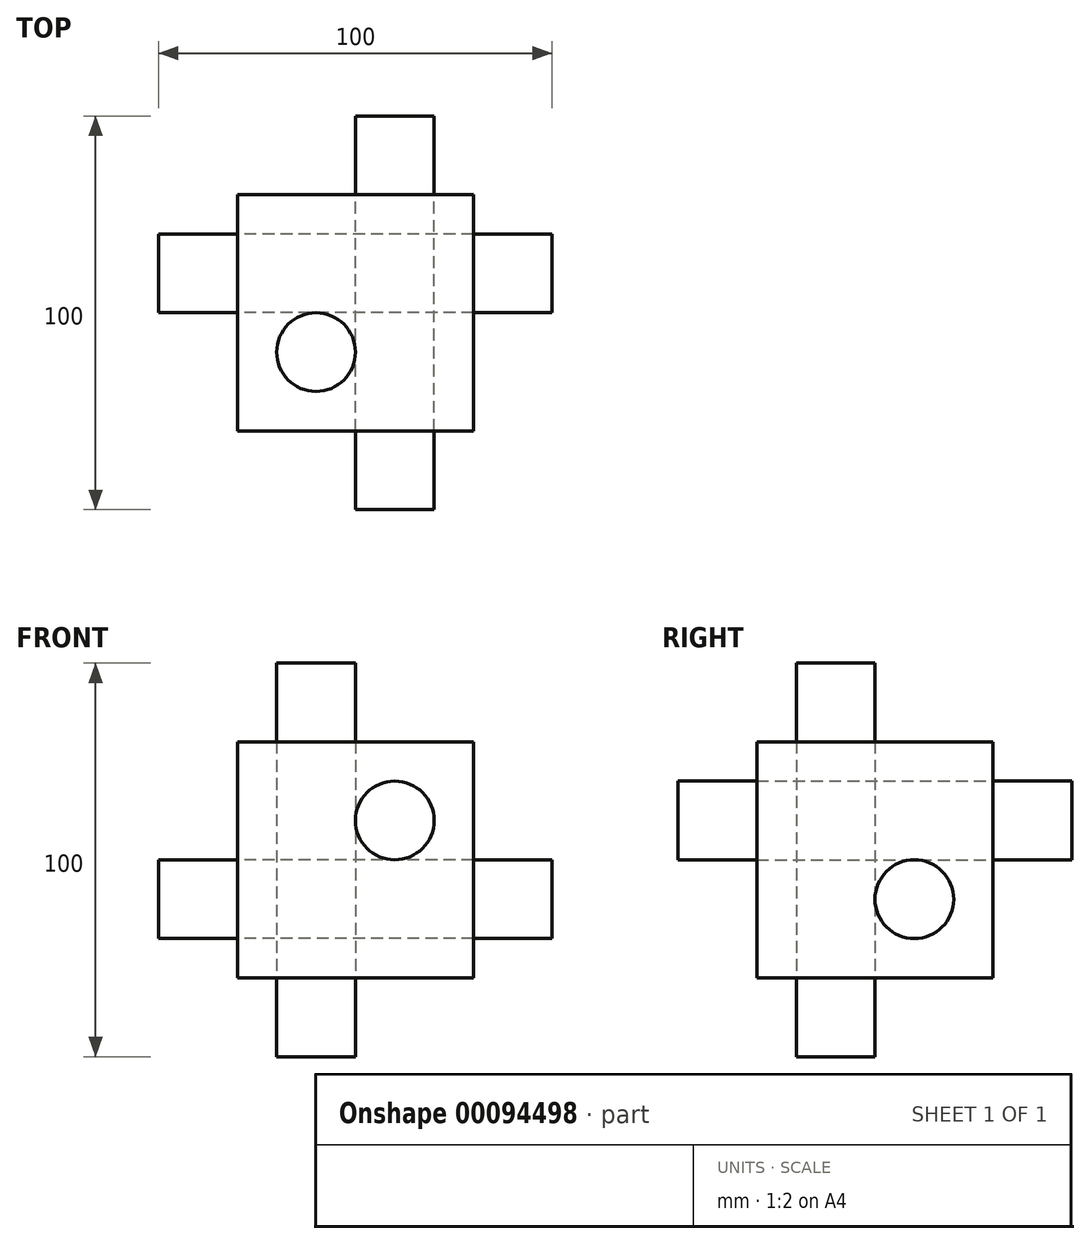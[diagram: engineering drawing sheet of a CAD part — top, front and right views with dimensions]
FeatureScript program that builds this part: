
annotation { "Feature Type Name" : "Feature", "Feature Type Description" : "" }
export const myFeature = defineFeature(function(context is Context, id is Id, definition is map)
    precondition{}
    {
        {
            var Q0;
            Q0=qCreatedBy(makeId("Top.planeOp"),FACE);
            var sketch = newSketch(context, id + "F0", { "sketchPlane" : qUnion([Q0])});
            skCircle(sketch, "E0", {"center": v(-10, -10) * mm, "radius": 10 * mm});
            skSolve(sketch);
        }
        {
            var Q0;
            Q0 = qSketchRegion(id + "F0", true);
            extrude(context, id + "F1", {"entities" : qUnion([Q0]), "endBound" : BoundingType.SYMMETRIC, "depth" : 100 * mm});
        }
        {
            var Q0;
            Q0=qCreatedBy(makeId("Front.planeOp"),FACE);
            var sketch = newSketch(context, id + "F2", { "sketchPlane" : qUnion([Q0])});
            skCircle(sketch, "E1", {"center": v(10, 10) * mm, "radius": 10 * mm});
            skSolve(sketch);
        }
        {
            var Q0;
            Q0 = qSketchRegion(id + "F2", true);
            extrude(context, id + "F3", {"entities" : qUnion([Q0]), "endBound" : BoundingType.SYMMETRIC, "depth" : 100 * mm});
        }
        {
            var Q0;
            Q0=qCreatedBy(makeId("Right.planeOp"),FACE);
            var sketch = newSketch(context, id + "F4", { "sketchPlane" : qUnion([Q0])});
            skCircle(sketch, "E2", {"center": v(10, -10) * mm, "radius": 10 * mm});
            skSolve(sketch);
        }
        {
            var Q0;
            Q0 = qSketchRegion(id + "F4", true);
            extrude(context, id + "F5", {"entities" : qUnion([Q0]), "endBound" : BoundingType.SYMMETRIC, "depth" : 100 * mm});
        }
        {
            var Q0;
            Q0=qCreatedBy(makeId("Right.planeOp"),FACE);
            var sketch = newSketch(context, id + "F6", { "sketchPlane" : qUnion([Q0])});
            skLineSegment(sketch, "E3.bottom", {"start": v(-30, 30) * mm, "end": v(30, 30) * mm});
            skLineSegment(sketch, "E3.top", {"start": v(-30, -30) * mm, "end": v(30, -30) * mm});
            skLineSegment(sketch, "E3.left", {"start": v(-30, 30) * mm, "end": v(-30, -30) * mm});
            skLineSegment(sketch, "E3.right", {"start": v(30, 30) * mm, "end": v(30, -30) * mm});
            skSolve(sketch);
        }
        {
            var Q0;
            Q0 = qSketchRegion(id + "F6", true);
            extrude(context, id + "F7", {"entities" : qUnion([Q0]), "endBound" : BoundingType.SYMMETRIC, "depth" : 60 * mm});
        }
    });
